# Revit family: Gira_117100
name_source: partatom
category: Electrical Fixtures
revit_build: Autodesk Revit 2017 (Build: 20160225_1515(x64)
units: mm (PartAtom-declared; Revit-internal decimal feet)

## family parameters
Cut with Voids When Loaded = No
Host = Face
Maintain Annotation Orientation = Yes
Part Type = Normal
Room Calculation Point = No
Round Connector Dimension = Use Diameter
Shared = No

## types (1)
- LED sig.light RD / GN System 55
    Available = No
    BIM (1) = https://media.stage.bim.site und Tasten.rfa?public/gira/36a6b08/Sys55_Komplettgerät_Schalten und Tasten.rfa
    Category = Monitored LED indicator luminaire
    Colour of lamp hood = Other
    Data sheet (1) = https://katalog.gira.de
    Default Elevation = 1219 mm
    Description = LED sig.light RD GN Sys55,LED signal light, 230 V~, red   green,,,Features:,- The signal lamp can be used for implementing easy signals for doctor's offices, conference rooms or hotel rooms, for example.,- The entire insert surface of 55 x 55 mm is divided into an upper half for the colour red and a lower half for the colour green with homogeneous illumination.,- The two halves can be activated separately, e.g. by using a series switch.
    GTIN = 4010337049289
    HAN = 117100
    HeinzeBIM = https://bimportal.heinze.de
    Manufacturer = Gira
    Manufacturer URL = https://www.gira.de
    Model = Sys55_Komplettgerät_Schalten und Tasten
    Name = LED sig.light RD / GN System 55
    Type of current = Ac
    URL = http://katalog.gira.de

## geometry (parser evidence)
native form markers: Blend x2, Sweep x6
no freeform markers — native parametric forms only
